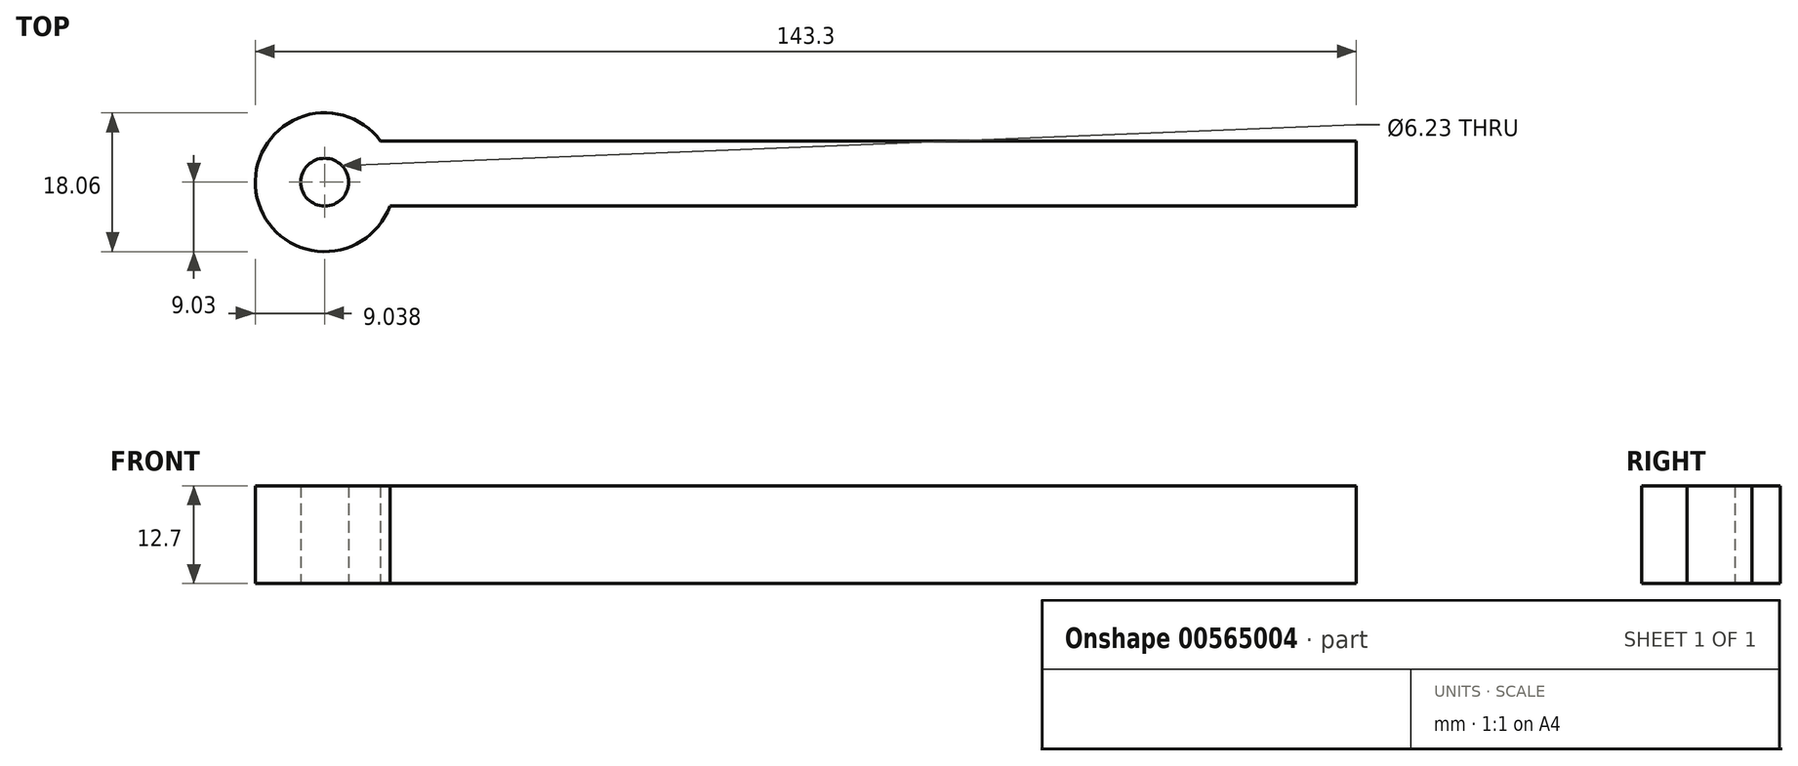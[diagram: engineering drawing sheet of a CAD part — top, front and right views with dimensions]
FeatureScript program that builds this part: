
annotation { "Feature Type Name" : "Feature", "Feature Type Description" : "" }
export const myFeature = defineFeature(function(context is Context, id is Id, definition is map)
    precondition{}
    {
        {
            var Q0;
            Q0=qCreatedBy(makeId("Top.planeOp"),FACE);
            var sketch = newSketch(context, id + "F0", { "sketchPlane" : qUnion([Q0])});
            skCircle(sketch, "E0", {"center": v(-68.22, 0) * mm, "radius": 9.03 * mm});
            skLineSegment(sketch, "E1", {"start": v(-60.96, 5.37) * mm, "end": v(66.04, 5.37) * mm});
            skLineSegment(sketch, "E2", {"start": v(66.04, 5.37) * mm, "end": v(66.04, -3.12) * mm});
            skLineSegment(sketch, "E3", {"start": v(66.04, -3.12) * mm, "end": v(-59.74, -3.12) * mm});
            skCircle(sketch, "E4", {"center": v(-68.22, 0) * mm, "radius": 3.12 * mm});
            skSolve(sketch);
        }
        {
            var Q0;
            Q0=makeQuery(id+"F0.imprint","IMPRINT",FACE,{"disambiguationData":[TD([[makeQuery(id+"F0.imprint","IMPRINT",EDGE,{"derivedFrom":sQuery(id+"F0.wireOp",EDGE,"E4")}),-1.0]])]});
            var Q1;
            {var subQ0=sQuery(id+"F0.wireOp",EDGE,"E1");Q1=makeQuery(id+"F0.imprint","IMPRINT",FACE,{"disambiguationData":[TD([[makeQuery(id+"F0.imprint","IMPRINT",EDGE,{"derivedFrom":subQ0}),-1.0]])]});}
            extrude(context, id + "F1", {"entities" : qUnion([Q0, Q1]), "depth" : 12.7 * mm, "offsetDistance" : 25.4 * mm});
        }
    });
